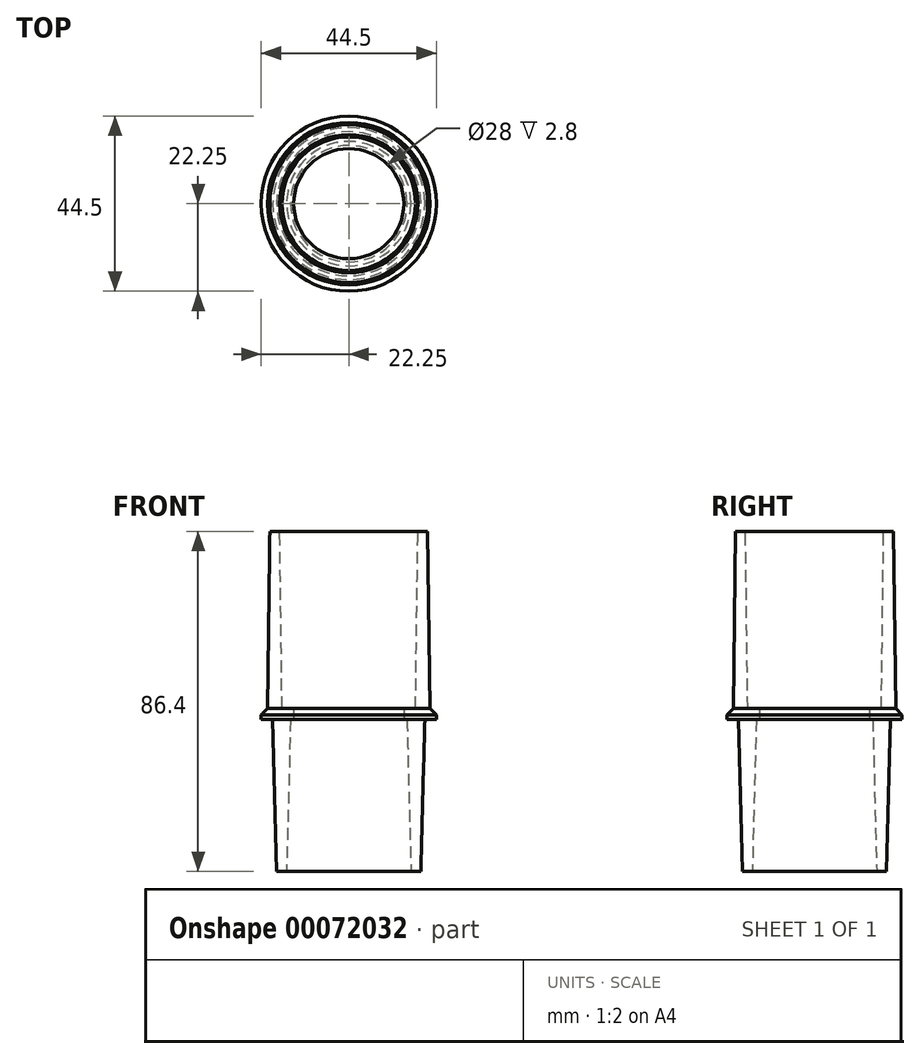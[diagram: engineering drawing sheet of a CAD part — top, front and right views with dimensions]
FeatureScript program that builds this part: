
annotation { "Feature Type Name" : "Feature", "Feature Type Description" : "" }
export const myFeature = defineFeature(function(context is Context, id is Id, definition is map)
    precondition{}
    {
        {
            var Q0;
            Q0=qCreatedBy(makeId("Top.planeOp"),FACE);
            var sketch = newSketch(context, id + "F0", { "sketchPlane" : qUnion([Q0])});
            skCircle(sketch, "E0", {"center": v(0, 0) * mm, "radius": 15 * mm});
            skCircle(sketch, "E1", {"center": v(0, 0) * mm, "radius": 17.5 * mm});
            skSolve(sketch);
        }
        {
            var Q0;
            Q0 = qSketchRegion(id + "F0", true);
            extrude(context, id + "F1", {"entities" : qUnion([Q0]), "depth" : 38.6 * mm, "hasDraft" : true, "draftAngle" : 1.5 * degree});
        }
        {
            var Q0;
            Q0=makeQuery(id+"F1.opExtrude","CAP_FACE",FACE,{"disambiguationData":[OSD([sQuery(id+"F0.wireOp",EDGE,"E0"),sQuery(id+"F0.wireOp",EDGE,"E1")])],"isStart":false});
            var sketch = newSketch(context, id + "F2", { "sketchPlane" : qUnion([Q0])});
            skCircle(sketch, "E2", {"center": v(0, 0) * mm, "radius": 14 * mm});
            skCircle(sketch, "E3", {"center": v(0, 0) * mm, "radius": 22.25 * mm});
            skSolve(sketch);
        }
        {
            var Q0;
            Q0=makeQuery(id+"F2.imprint","IMPRINT",FACE,{"disambiguationData":[TD([[makeQuery(id+"F2.imprint","IMPRINT",EDGE,{"derivedFrom":sQuery(id+"F2.wireOp",EDGE,"E3")}),1.0]])]});
            var Q1;
            Q1=makeQuery(id+"F2.imprint","IMPRINT",FACE,{"disambiguationData":[TD([[makeQuery(id+"F2.imprint","IMPRINT",EDGE,{"derivedFrom":sQuery(id+"F2.wireOp",EDGE,"E2")}),-1.0]])]});
            extrude(context, id + "F3", {"entities" : qUnion([Q0, Q1]), "operationType" : NewBodyOperationType.ADD, "depth" : 2.8 * mm});
        }
        {
            var Q0;
            Q0=makeQuery(id+"F3.opExtrude","CAP_FACE",FACE,{"disambiguationData":[OSD([sQuery(id+"F2.wireOp",EDGE,"E2"),sQuery(id+"F2.wireOp",EDGE,"E3")])],"isStart":false});
            cPlane(context, id + "F4", {"entities" : qUnion([Q0]), "cplaneType" : CPlaneType.OFFSET, "offset" : 45 * mm, "width" : 150 * mm, "height" : 150 * mm});
        }
        {
            var Q0;
            Q0=qCreatedBy(id+"F4.planeOp",FACE);
            var sketch = newSketch(context, id + "F5", { "sketchPlane" : qUnion([Q0])});
            skCircle(sketch, "E4", {"center": v(0, 0) * mm, "radius": 17.55 * mm});
            skCircle(sketch, "E5", {"center": v(0, 0) * mm, "radius": 20.05 * mm});
            skSolve(sketch);
        }
        {
            var Q0;
            Q0 = qSketchRegion(id + "F5", true);
            var Q1;
            Q1=makeQuery(id+"F1.opExtrude","SWEPT_BODY",BODY,{"disambiguationData":[OSD([sQuery(id+"F0.wireOp",EDGE,"E0"),sQuery(id+"F0.wireOp",EDGE,"E1")])]});
            extrude(context, id + "F6", {"entities" : qUnion([Q0]), "operationType" : NewBodyOperationType.ADD, "endBound" : BoundingType.UP_TO_BODY, "oppositeDirection" : true, "endBoundEntityBody" : qUnion([Q1]), "depth" : 25 * mm, "hasDraft" : true, "draftAngle" : .75 * degree});
        }
        {
            var Q0;
            Q0=makeQuery(id+"F3.opExtrude","CAP_EDGE",EDGE,{"disambiguationData":[OSD([sQuery(id+"F2.wireOp",EDGE,"E3")])],"isStart":false});
            chamfer(context, id + "F7", {"entities" : qUnion([Q0]), "width" : 1.61 * mm, "tangentPropagation" : true});
        }
        {
            var Q0;
            Q0=qCreatedBy(makeId("Top.planeOp"),FACE);
            var sketch = newSketch(context, id + "F8", { "sketchPlane" : qUnion([Q0])});
            skCircle(sketch, "E6", {"center": v(0, 0) * mm, "radius": 31.61 * mm});
            skSolve(sketch);
        }
        {
            var Q0;
            Q0 = qSketchRegion(id + "F8", true);
            var Q1;
            Q1=makeQuery(id+"F3.opExtrude","CAP_FACE",FACE,{"disambiguationData":[OSD([sQuery(id+"F2.wireOp",EDGE,"E2"),sQuery(id+"F2.wireOp",EDGE,"E3")])],"isStart":true});
            extrude(context, id + "F9", {"entities" : qUnion([Q0]), "operationType" : NewBodyOperationType.REMOVE, "endBound" : BoundingType.UP_TO_SURFACE, "endBoundEntityFace" : qUnion([Q1]), "depth" : 25 * mm});
        }
        {
            var Q0;
            Q0=qCreatedBy(makeId("Top.planeOp"),FACE);
            var sketch = newSketch(context, id + "F10", { "sketchPlane" : qUnion([Q0])});
            skCircle(sketch, "E7", {"center": v(0, 0) * mm, "radius": 18.3 * mm});
            skCircle(sketch, "E8", {"center": v(0, 0) * mm, "radius": 15.8 * mm});
            skSolve(sketch);
        }
        {
            var Q0;
            Q0 = qSketchRegion(id + "F10", true);
            var Q1;
            {var subQ0=sQuery(id+"F2.wireOp",EDGE,"E3");var subQ1=sQuery(id+"F2.wireOp",EDGE,"E2");Q1=makeQuery(id+"F9.boolean.opBoolean","MERGE",FACE,{"derivedFrom":[makeQuery(id+"F3.opExtrude","CAP_FACE",FACE,{"disambiguationData":[OSD([subQ1,subQ0])],"isStart":true}),makeQuery(id+"F9.opExtrude","CAP_FACE",FACE,{"disambiguationData":[OSD([subQ1,subQ0])],"isStart":false})]});}
            extrude(context, id + "F11", {"entities" : qUnion([Q0]), "operationType" : NewBodyOperationType.ADD, "endBound" : BoundingType.UP_TO_SURFACE, "endBoundEntityFace" : qUnion([Q1]), "depth" : 25 * mm, "hasDraft" : true, "draftAngle" : 1.5 * degree});
        }
    });
